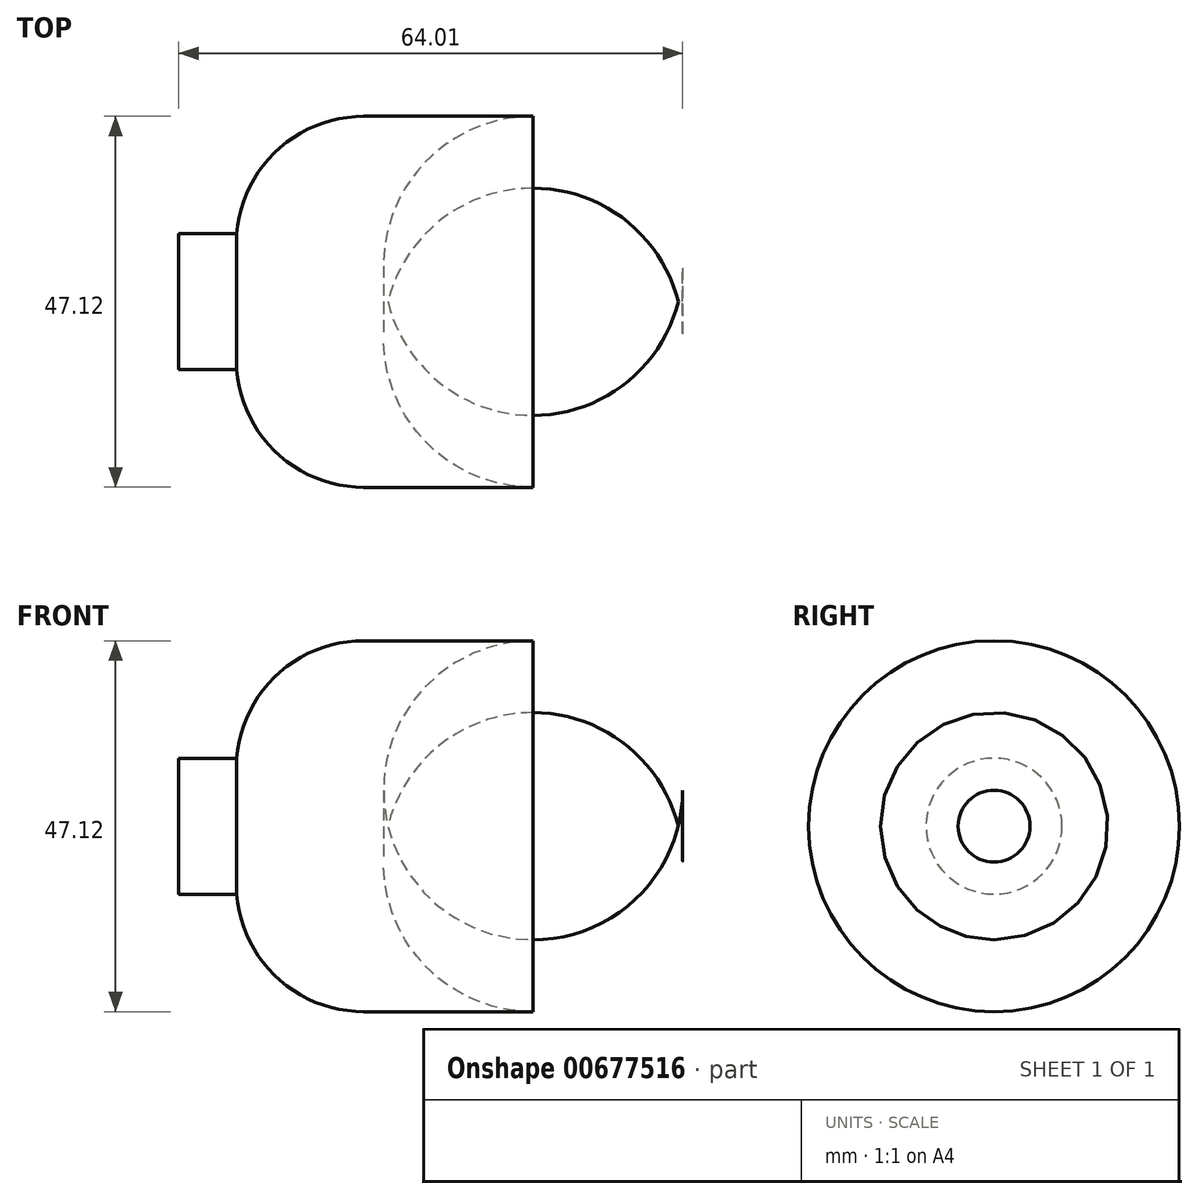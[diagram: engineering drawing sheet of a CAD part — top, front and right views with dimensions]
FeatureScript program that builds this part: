
annotation { "Feature Type Name" : "Feature", "Feature Type Description" : "" }
export const myFeature = defineFeature(function(context is Context, id is Id, definition is map)
    precondition{}
    {
        {
            var Q0;
            Q0=qCreatedBy(makeId("Front.planeOp"),FACE);
            var sketch = newSketch(context, id + "F0", { "sketchPlane" : qUnion([Q0])});
            skLineSegment(sketch, "E0", {"start": v(54.63, 0) * mm, "end": v(118.64, 0) * mm});
            skLineSegment(sketch, "E1", {"start": v(54.63, 0) * mm, "end": v(54.63, 8.64) * mm});
            skLineSegment(sketch, "E2", {"start": v(54.63, 8.64) * mm, "end": v(62, 8.64) * mm});
            skLineSegment(sketch, "E3", {"start": v(78.12, 23.56) * mm, "end": v(99.64, 23.56) * mm});
            skLineSegment(sketch, "E4", {"start": v(118.64, 4.56) * mm, "end": v(118.64, 0) * mm});
            skPoint(sketch, "E5.visualSharp", {"position": v(118.64, 23.56) * mm});
            skArc(sketch, "E5.filletArc", {"start": v(118.64, 4.56) * mm, "mid": v(113.07, 18) * mm, "end": v(99.64, 23.56) * mm});
            skArc(sketch, "E6", {"start": v(78.12, 23.56) * mm, "mid": v(67.13, 19.26) * mm, "end": v(62, 8.64) * mm});
            skSolve(sketch);
        }
        {
            var Q0;
            Q0=makeQuery(id+"F0.imprint","IMPRINT",FACE,{"disambiguationData":[TD([[makeQuery(id+"F0.imprint","IMPRINT",EDGE,{"derivedFrom":sQuery(id+"F0.wireOp",EDGE,"E0")}),1.0]])]});
            var Q1;
            Q1=sQuery(id+"F0.wireOp",EDGE,"E0");
            revolve(context, id + "F1", {"entities" : qUnion([Q0]), "axis" : qUnion([Q1]), "revolveType" : RevolveType.FULL});
        }
    });
